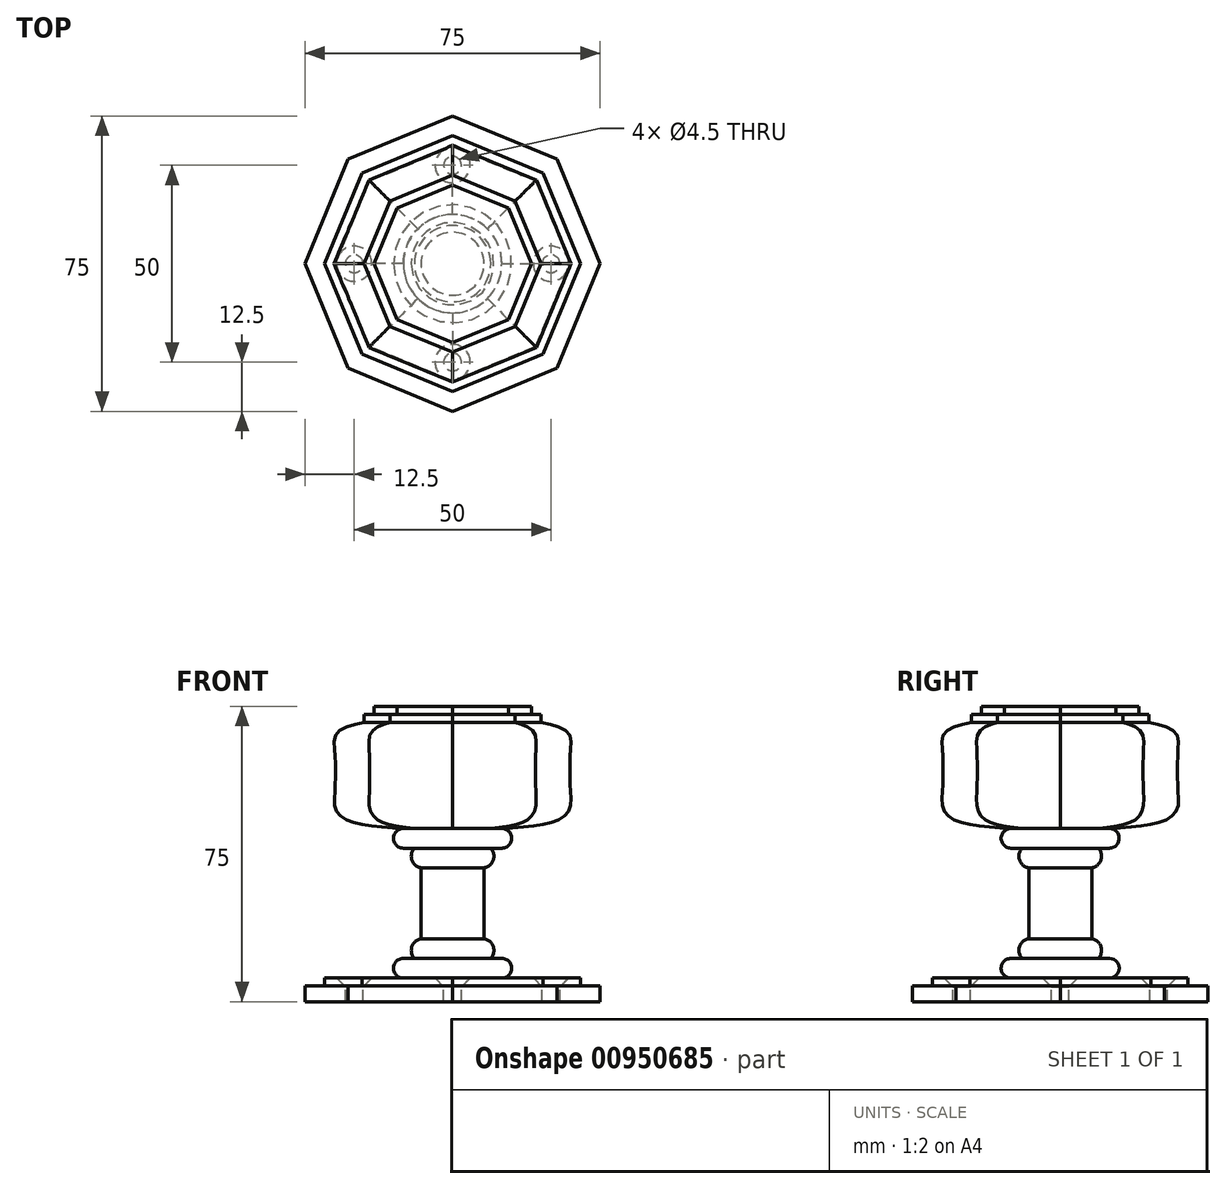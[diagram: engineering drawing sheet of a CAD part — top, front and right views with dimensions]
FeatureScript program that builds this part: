
annotation { "Feature Type Name" : "Feature", "Feature Type Description" : "" }
export const myFeature = defineFeature(function(context is Context, id is Id, definition is map)
    precondition{}
    {
        {
            var Q0;
            Q0=qCreatedBy(makeId("Top.planeOp"),FACE);
            var sketch = newSketch(context, id + "F0", { "sketchPlane" : qUnion([Q0])});
            skCircle(sketch, "E0.cCircle", {"center": v(0, 0) * mm, "radius": 37.5 * mm, "construction": true});
            skLineSegment(sketch, "E0.0", {"start": v(37.5, 0) * mm, "end": v(26.52, -26.52) * mm});
            skLineSegment(sketch, "E0.1", {"start": v(26.52, -26.52) * mm, "end": v(0, -37.5) * mm});
            skLineSegment(sketch, "E0.2", {"start": v(0, -37.5) * mm, "end": v(-26.52, -26.52) * mm});
            skLineSegment(sketch, "E0.3", {"start": v(-26.52, -26.52) * mm, "end": v(-37.5, 0) * mm});
            skLineSegment(sketch, "E0.4", {"start": v(-37.5, 0) * mm, "end": v(-26.52, 26.52) * mm});
            skLineSegment(sketch, "E0.5", {"start": v(-26.52, 26.52) * mm, "end": v(0, 37.5) * mm});
            skLineSegment(sketch, "E0.6", {"start": v(0, 37.5) * mm, "end": v(26.52, 26.52) * mm});
            skLineSegment(sketch, "E0.7", {"start": v(26.52, 26.52) * mm, "end": v(37.5, 0) * mm});
            skSolve(sketch);
        }
        {
            var Q0;
            Q0=makeQuery(id+"F0.imprint","IMPRINT",FACE,{"disambiguationData":[TD([[makeQuery(id+"F0.imprint","IMPRINT",EDGE,{"derivedFrom":sQuery(id+"F0.wireOp",EDGE,"E0.0")}),-1.0]])]});
            extrude(context, id + "F1", {"entities" : qUnion([Q0]), "depth" : 4 * mm, "offsetDistance" : 25 * mm});
        }
        {
            var Q0;
            Q0=makeQuery(id+"F1.opExtrude","CAP_FACE",FACE,{"disambiguationData":[OSD([sQuery(id+"F0.wireOp",EDGE,"E0.0"),sQuery(id+"F0.wireOp",EDGE,"E0.1"),sQuery(id+"F0.wireOp",EDGE,"E0.2"),sQuery(id+"F0.wireOp",EDGE,"E0.3"),sQuery(id+"F0.wireOp",EDGE,"E0.4"),sQuery(id+"F0.wireOp",EDGE,"E0.5"),sQuery(id+"F0.wireOp",EDGE,"E0.6"),sQuery(id+"F0.wireOp",EDGE,"E0.7")])],"isStart":false});
            var sketch = newSketch(context, id + "F2", { "sketchPlane" : qUnion([Q0])});
            skCircle(sketch, "E1.cCircle", {"center": v(0, 0) * mm, "radius": 32.5 * mm, "construction": true});
            skLineSegment(sketch, "E1.0", {"start": v(32.5, 0) * mm, "end": v(22.98, -22.98) * mm});
            skLineSegment(sketch, "E1.1", {"start": v(22.98, -22.98) * mm, "end": v(0, -32.5) * mm});
            skLineSegment(sketch, "E1.2", {"start": v(0, -32.5) * mm, "end": v(-22.98, -22.98) * mm});
            skLineSegment(sketch, "E1.3", {"start": v(-22.98, -22.98) * mm, "end": v(-32.5, 0) * mm});
            skLineSegment(sketch, "E1.4", {"start": v(-32.5, 0) * mm, "end": v(-22.98, 22.98) * mm});
            skLineSegment(sketch, "E1.5", {"start": v(-22.98, 22.98) * mm, "end": v(0, 32.5) * mm});
            skLineSegment(sketch, "E1.6", {"start": v(0, 32.5) * mm, "end": v(22.98, 22.98) * mm});
            skLineSegment(sketch, "E1.7", {"start": v(22.98, 22.98) * mm, "end": v(32.5, 0) * mm});
            skSolve(sketch);
        }
        {
            var Q0;
            Q0=makeQuery(id+"F2.imprint","IMPRINT",FACE,{"disambiguationData":[TD([[makeQuery(id+"F2.imprint","IMPRINT",EDGE,{"derivedFrom":sQuery(id+"F2.wireOp",EDGE,"E1.0")}),-1.0]])]});
            extrude(context, id + "F3", {"entities" : qUnion([Q0]), "operationType" : NewBodyOperationType.ADD, "depth" : 2 * mm, "offsetDistance" : 25 * mm});
        }
        {
            var Q0;
            Q0=qCreatedBy(makeId("Front.planeOp"),FACE);
            var sketch = newSketch(context, id + "F4", { "sketchPlane" : qUnion([Q0])});
            skLineSegment(sketch, "E2", {"start": v(0, 0) * mm, "end": v(0, 93.5) * mm, "construction": true});
            skLineSegment(sketch, "E3", {"start": v(8, 34) * mm, "end": v(8, 16) * mm});
            skLineSegment(sketch, "E4", {"start": v(12.5, 6) * mm, "end": v(0, 6) * mm});
            skLineSegment(sketch, "E5", {"start": v(8, 25) * mm, "end": v(0, 25) * mm, "construction": true});
            skLineSegment(sketch, "E6", {"start": v(0, 6) * mm, "end": v(0, 44) * mm});
            skLineSegment(sketch, "E7", {"start": v(9.7, 11) * mm, "end": v(12.5, 11) * mm});
            skArc(sketch, "E8", {"start": v(12.5, 6) * mm, "mid": v(15, 8.5) * mm, "end": v(12.5, 11) * mm});
            skArc(sketch, "E9", {"start": v(9.7, 11) * mm, "mid": v(10.34, 14) * mm, "end": v(8, 16) * mm});
            skArc(sketch, "E10.MirrorCS", {"start": v(9.7, 39) * mm, "mid": v(10.34, 36) * mm, "end": v(8, 34) * mm});
            skLineSegment(sketch, "E11.MirrorCS", {"start": v(9.7, 39) * mm, "end": v(12.5, 39) * mm});
            skArc(sketch, "E12.MirrorCS", {"start": v(12.5, 44) * mm, "mid": v(15, 41.5) * mm, "end": v(12.5, 39) * mm});
            skLineSegment(sketch, "E13", {"start": v(0, 44) * mm, "end": v(12.5, 44) * mm});
            skSolve(sketch);
        }
        {
            var Q0;
            Q0=makeQuery(id+"F4.imprint","IMPRINT",FACE,{"disambiguationData":[TD([[makeQuery(id+"F4.imprint","IMPRINT",EDGE,{"derivedFrom":sQuery(id+"F4.wireOp",EDGE,"E3")}),-1.0]])]});
            var Q1;
            Q1=sQuery(id+"F4.wireOp",EDGE,"E2");
            revolve(context, id + "F5", {"operationType" : NewBodyOperationType.ADD, "surfaceOperationType" : NewSurfaceOperationType.NEW, "entities" : qUnion([Q0]), "axis" : qUnion([Q1]), "revolveType" : RevolveType.FULL});
        }
        {
            var Q0;
            Q0=makeQuery(id+"F5.opRevolve","SWEPT_FACE",FACE,{"disambiguationData":[OSD([sQuery(id+"F4.wireOp",EDGE,"E13")])]});
            var sketch = newSketch(context, id + "F6", { "sketchPlane" : qUnion([Q0])});
            skCircle(sketch, "E14.0", {"center": v(0, 0) * mm, "radius": 12.5 * mm});
            skSolve(sketch);
        }
        {
            var Q0;
            Q0=makeQuery(id+"F5.opRevolve","SWEPT_FACE",FACE,{"disambiguationData":[OSD([sQuery(id+"F4.wireOp",EDGE,"E13")])]});
            cPlane(context, id + "F7", {"entities" : qUnion([Q0]), "cplaneType" : CPlaneType.OFFSET, "offset" : 6 * mm, "width" : 150 * mm, "height" : 150 * mm});
        }
        {
            var Q0;
            Q0=qCreatedBy(id+"F7.planeOp",FACE);
            var sketch = newSketch(context, id + "F8", { "sketchPlane" : qUnion([Q0])});
            skCircle(sketch, "E15.cCircle", {"center": v(0, 0) * mm, "radius": 30 * mm, "construction": true});
            skLineSegment(sketch, "E15.0", {"start": v(30, 0) * mm, "end": v(21.21, -21.21) * mm});
            skLineSegment(sketch, "E15.1", {"start": v(21.21, -21.21) * mm, "end": v(0, -30) * mm});
            skLineSegment(sketch, "E15.2", {"start": v(0, -30) * mm, "end": v(-21.21, -21.21) * mm});
            skLineSegment(sketch, "E15.3", {"start": v(-21.21, -21.21) * mm, "end": v(-30, 0) * mm});
            skLineSegment(sketch, "E15.4", {"start": v(-30, 0) * mm, "end": v(-21.21, 21.21) * mm});
            skLineSegment(sketch, "E15.5", {"start": v(-21.21, 21.21) * mm, "end": v(0, 30) * mm});
            skLineSegment(sketch, "E15.6", {"start": v(0, 30) * mm, "end": v(21.21, 21.21) * mm});
            skLineSegment(sketch, "E15.7", {"start": v(21.21, 21.21) * mm, "end": v(30, 0) * mm});
            skSolve(sketch);
        }
        {
            var Q0;
            Q0=qCreatedBy(id+"F7.planeOp",FACE);
            cPlane(context, id + "F9", {"entities" : qUnion([Q0]), "cplaneType" : CPlaneType.OFFSET, "offset" : 2 * mm, "width" : 150 * mm, "height" : 150 * mm});
        }
        {
            var Q0;
            Q0=qCreatedBy(id+"F9.planeOp",FACE);
            var sketch = newSketch(context, id + "F10", { "sketchPlane" : qUnion([Q0])});
            skCircle(sketch, "E16.0", {"center": v(0, 0) * mm, "radius": 30 * mm});
            skLineSegment(sketch, "E16.1", {"start": v(30, 0) * mm, "end": v(21.21, -21.21) * mm});
            skLineSegment(sketch, "E16.2", {"start": v(21.21, -21.21) * mm, "end": v(0, -30) * mm});
            skLineSegment(sketch, "E16.3", {"start": v(0, -30) * mm, "end": v(-21.21, -21.21) * mm});
            skLineSegment(sketch, "E16.4", {"start": v(-21.21, -21.21) * mm, "end": v(-30, 0) * mm});
            skLineSegment(sketch, "E16.5", {"start": v(-30, 0) * mm, "end": v(-21.21, 21.21) * mm});
            skLineSegment(sketch, "E16.6", {"start": v(-21.21, 21.21) * mm, "end": v(0, 30) * mm});
            skLineSegment(sketch, "E16.7", {"start": v(0, 30) * mm, "end": v(21.21, 21.21) * mm});
            skLineSegment(sketch, "E16.8", {"start": v(21.21, 21.21) * mm, "end": v(30, 0) * mm});
            skSolve(sketch);
        }
        {
            var Q0;
            Q0=qCreatedBy(id+"F7.planeOp",FACE);
            cPlane(context, id + "F11", {"entities" : qUnion([Q0]), "cplaneType" : CPlaneType.OFFSET, "offset" : 15 * mm, "width" : 150 * mm, "height" : 150 * mm});
        }
        {
            var Q0;
            Q0=qCreatedBy(id+"F11.planeOp",FACE);
            var sketch = newSketch(context, id + "F12", { "sketchPlane" : qUnion([Q0])});
            skCircle(sketch, "E17.0", {"center": v(0, 0) * mm, "radius": 30 * mm});
            skLineSegment(sketch, "E17.1", {"start": v(30, 0) * mm, "end": v(21.21, -21.21) * mm});
            skLineSegment(sketch, "E17.2", {"start": v(21.21, -21.21) * mm, "end": v(0, -30) * mm});
            skLineSegment(sketch, "E17.3", {"start": v(0, -30) * mm, "end": v(-21.21, -21.21) * mm});
            skLineSegment(sketch, "E17.4", {"start": v(-21.21, -21.21) * mm, "end": v(-30, 0) * mm});
            skLineSegment(sketch, "E17.5", {"start": v(-30, 0) * mm, "end": v(-21.21, 21.21) * mm});
            skLineSegment(sketch, "E17.6", {"start": v(-21.21, 21.21) * mm, "end": v(0, 30) * mm});
            skLineSegment(sketch, "E17.7", {"start": v(0, 30) * mm, "end": v(21.21, 21.21) * mm});
            skLineSegment(sketch, "E17.8", {"start": v(21.21, 21.21) * mm, "end": v(30, 0) * mm});
            skSolve(sketch);
        }
        {
            var Q0;
            Q0=qCreatedBy(id+"F11.planeOp",FACE);
            cPlane(context, id + "F13", {"entities" : qUnion([Q0]), "cplaneType" : CPlaneType.OFFSET, "offset" : 2 * mm, "width" : 150 * mm, "height" : 150 * mm});
        }
        {
            var Q0;
            Q0=qCreatedBy(id+"F13.planeOp",FACE);
            var sketch = newSketch(context, id + "F14", { "sketchPlane" : qUnion([Q0])});
            skCircle(sketch, "E18.0", {"center": v(0, 0) * mm, "radius": 30 * mm});
            skLineSegment(sketch, "E18.1", {"start": v(30, 0) * mm, "end": v(21.21, -21.21) * mm});
            skLineSegment(sketch, "E18.2", {"start": v(21.21, -21.21) * mm, "end": v(0, -30) * mm});
            skLineSegment(sketch, "E18.3", {"start": v(0, -30) * mm, "end": v(-21.21, -21.21) * mm});
            skLineSegment(sketch, "E18.4", {"start": v(-21.21, -21.21) * mm, "end": v(-30, 0) * mm});
            skLineSegment(sketch, "E18.5", {"start": v(-30, 0) * mm, "end": v(-21.21, 21.21) * mm});
            skLineSegment(sketch, "E18.6", {"start": v(-21.21, 21.21) * mm, "end": v(0, 30) * mm});
            skLineSegment(sketch, "E18.7", {"start": v(0, 30) * mm, "end": v(21.21, 21.21) * mm});
            skLineSegment(sketch, "E18.8", {"start": v(21.21, 21.21) * mm, "end": v(30, 0) * mm});
            skSolve(sketch);
        }
        {
            var Q0;
            Q0=qCreatedBy(id+"F11.planeOp",FACE);
            cPlane(context, id + "F15", {"entities" : qUnion([Q0]), "cplaneType" : CPlaneType.OFFSET, "offset" : 6 * mm, "width" : 150 * mm, "height" : 150 * mm});
        }
        {
            var Q0;
            Q0=qCreatedBy(id+"F15.planeOp",FACE);
            var sketch = newSketch(context, id + "F16", { "sketchPlane" : qUnion([Q0])});
            skCircle(sketch, "E19.cCircle", {"center": v(0, 0) * mm, "radius": 22.5 * mm, "construction": true});
            skLineSegment(sketch, "E19.0", {"start": v(22.5, 0) * mm, "end": v(15.9, -15.9) * mm});
            skLineSegment(sketch, "E19.1", {"start": v(15.9, -15.9) * mm, "end": v(0, -22.5) * mm});
            skLineSegment(sketch, "E19.2", {"start": v(0, -22.5) * mm, "end": v(-15.9, -15.9) * mm});
            skLineSegment(sketch, "E19.3", {"start": v(-15.9, -15.9) * mm, "end": v(-22.5, 0) * mm});
            skLineSegment(sketch, "E19.4", {"start": v(-22.5, 0) * mm, "end": v(-15.9, 15.9) * mm});
            skLineSegment(sketch, "E19.5", {"start": v(-15.9, 15.9) * mm, "end": v(0, 22.5) * mm});
            skLineSegment(sketch, "E19.6", {"start": v(0, 22.5) * mm, "end": v(15.9, 15.9) * mm});
            skLineSegment(sketch, "E19.7", {"start": v(15.9, 15.9) * mm, "end": v(22.5, 0) * mm});
            skSolve(sketch);
        }
        {
            var Q1;
            Q1 = qSketchRegion(id + "F6", true);
            var Q2;
            Q2=makeQuery(id+"F8.imprint","IMPRINT",FACE,{"disambiguationData":[TD([[makeQuery(id+"F8.imprint","IMPRINT",EDGE,{"derivedFrom":sQuery(id+"F8.wireOp",EDGE,"E15.0")}),-1.0]])]});
            var Q3;
            Q3=makeQuery(id+"F10.imprint","IMPRINT",FACE,{"disambiguationData":[TD([[makeQuery(id+"F10.imprint","IMPRINT",EDGE,{"derivedFrom":sQuery(id+"F10.wireOp",EDGE,"E16.1")}),-1.0]])]});
            var Q4;
            Q4=makeQuery(id+"F12.imprint","IMPRINT",FACE,{"disambiguationData":[TD([[makeQuery(id+"F12.imprint","IMPRINT",EDGE,{"derivedFrom":sQuery(id+"F12.wireOp",EDGE,"E17.1")}),-1.0]])]});
            var Q5;
            Q5=makeQuery(id+"F14.imprint","IMPRINT",FACE,{"disambiguationData":[TD([[makeQuery(id+"F14.imprint","IMPRINT",EDGE,{"derivedFrom":sQuery(id+"F14.wireOp",EDGE,"E18.1")}),-1.0]])]});
            var Q6;
            Q6=makeQuery(id+"F16.imprint","IMPRINT",FACE,{"disambiguationData":[TD([[makeQuery(id+"F16.imprint","IMPRINT",EDGE,{"derivedFrom":sQuery(id+"F16.wireOp",EDGE,"E19.0")}),-1.0]])]});
            loft(context, id + "F17", {"operationType" : NewBodyOperationType.ADD, "sheetProfilesArray" : [{ "sheetProfileEntities" : qUnion([Q1]) }, { "sheetProfileEntities" : qUnion([Q2]) }, { "sheetProfileEntities" : qUnion([Q3]) }, { "sheetProfileEntities" : qUnion([Q4]) }, { "sheetProfileEntities" : qUnion([Q5]) }, { "sheetProfileEntities" : qUnion([Q6]) }]});
        }
        {
            var Q0;
            Q0 = qSketchRegion(id + "F16", true);
            extrude(context, id + "F18", {"entities" : qUnion([Q0]), "operationType" : NewBodyOperationType.ADD, "depth" : 2 * mm, "offsetDistance" : 25 * mm});
        }
        {
            var Q0;
            Q0=makeQuery(id+"F18.opExtrude","CAP_FACE",FACE,{"disambiguationData":[OSD([sQuery(id+"F16.wireOp",EDGE,"E19.0"),sQuery(id+"F16.wireOp",EDGE,"E19.1"),sQuery(id+"F16.wireOp",EDGE,"E19.2"),sQuery(id+"F16.wireOp",EDGE,"E19.3"),sQuery(id+"F16.wireOp",EDGE,"E19.4"),sQuery(id+"F16.wireOp",EDGE,"E19.5"),sQuery(id+"F16.wireOp",EDGE,"E19.6"),sQuery(id+"F16.wireOp",EDGE,"E19.7")])],"isStart":false});
            var sketch = newSketch(context, id + "F19", { "sketchPlane" : qUnion([Q0])});
            skCircle(sketch, "E20.cCircle", {"center": v(0, 0) * mm, "radius": 20 * mm, "construction": true});
            skLineSegment(sketch, "E20.0", {"start": v(20, 0) * mm, "end": v(14.14, -14.14) * mm});
            skLineSegment(sketch, "E20.1", {"start": v(14.14, -14.14) * mm, "end": v(0, -20) * mm});
            skLineSegment(sketch, "E20.2", {"start": v(0, -20) * mm, "end": v(-14.14, -14.14) * mm});
            skLineSegment(sketch, "E20.3", {"start": v(-14.14, -14.14) * mm, "end": v(-20, 0) * mm});
            skLineSegment(sketch, "E20.4", {"start": v(-20, 0) * mm, "end": v(-14.14, 14.14) * mm});
            skLineSegment(sketch, "E20.5", {"start": v(-14.14, 14.14) * mm, "end": v(0, 20) * mm});
            skLineSegment(sketch, "E20.6", {"start": v(0, 20) * mm, "end": v(14.14, 14.14) * mm});
            skLineSegment(sketch, "E20.7", {"start": v(14.14, 14.14) * mm, "end": v(20, 0) * mm});
            skSolve(sketch);
        }
        {
            var Q0;
            Q0=makeQuery(id+"F19.imprint","IMPRINT",FACE,{"disambiguationData":[TD([[makeQuery(id+"F19.imprint","IMPRINT",EDGE,{"derivedFrom":sQuery(id+"F19.wireOp",EDGE,"E20.0")}),-1.0]])]});
            extrude(context, id + "F20", {"entities" : qUnion([Q0]), "operationType" : NewBodyOperationType.ADD, "depth" : 2 * mm, "offsetDistance" : 25 * mm});
        }
        {
            var Q0;
            Q0=makeQuery(id+"F3.opExtrude","CAP_FACE",FACE,{"disambiguationData":[OSD([sQuery(id+"F2.wireOp",EDGE,"E1.0"),sQuery(id+"F2.wireOp",EDGE,"E1.1"),sQuery(id+"F2.wireOp",EDGE,"E1.2"),sQuery(id+"F2.wireOp",EDGE,"E1.3"),sQuery(id+"F2.wireOp",EDGE,"E1.4"),sQuery(id+"F2.wireOp",EDGE,"E1.5"),sQuery(id+"F2.wireOp",EDGE,"E1.6"),sQuery(id+"F2.wireOp",EDGE,"E1.7")])],"isStart":false});
            var sketch = newSketch(context, id + "F21", { "sketchPlane" : qUnion([Q0])});
            skPoint(sketch, "E21", {"position": v(-25, 0) * mm});
            skCircle(sketch, "E22", {"center": v(0, 0) * mm, "radius": 25 * mm, "construction": true});
            skPoint(sketch, "E23", {"position": v(25, 0) * mm});
            skPoint(sketch, "E24", {"position": v(0, 25) * mm});
            skPoint(sketch, "E25", {"position": v(0, -25) * mm});
            skSolve(sketch);
        }
        {
            var Q0;
            Q0=sQuery(id+"F21.wireOp",VERTEX,"E21");
            var Q1;
            Q1=sQuery(id+"F21.wireOp",VERTEX,"E25");
            var Q2;
            Q2=sQuery(id+"F21.wireOp",VERTEX,"E23");
            var Q3;
            Q3=sQuery(id+"F21.wireOp",VERTEX,"E24");
            var Q4;
            Q4=makeQuery(id+"F1.opExtrude","SWEPT_BODY",BODY,{"disambiguationData":[OSD([sQuery(id+"F0.wireOp",EDGE,"E0.0"),sQuery(id+"F0.wireOp",EDGE,"E0.1"),sQuery(id+"F0.wireOp",EDGE,"E0.2"),sQuery(id+"F0.wireOp",EDGE,"E0.3"),sQuery(id+"F0.wireOp",EDGE,"E0.4"),sQuery(id+"F0.wireOp",EDGE,"E0.5"),sQuery(id+"F0.wireOp",EDGE,"E0.6"),sQuery(id+"F0.wireOp",EDGE,"E0.7")])]});
            hole(context, id + "F22", {"style" : HoleStyle.C_SINK, "endStyle" : HoleEndStyle.BLIND, "standardTappedOrClearance" : lookupTablePath({ "fit" : "Normal", "standard" : "ISO", "size" : "M4", "type" : "Clearance" }), "standardBlindInLast" : lookupTablePath({ "fit" : "Normal", "standard" : "ISO", "engagement" : "75%", "pitch" : "0.7 mm", "size" : "M4", "type" : "Clearance & tapped" }), "holeDiameter" : 4.5 * mm, "cSinkDiameter" : 8.96 * mm, "cSinkAngle" : 90 * degree, "majorDiameter" : 4 * mm, "holeDepth" : 8 * mm, "isTappedThrough" : true, "tappedDepth" : 5.9 * mm, "tapClearance" : 3, "locations" : qUnion([Q0, Q1, Q2, Q3]), "scope" : qUnion([Q4])});
        }
    });
